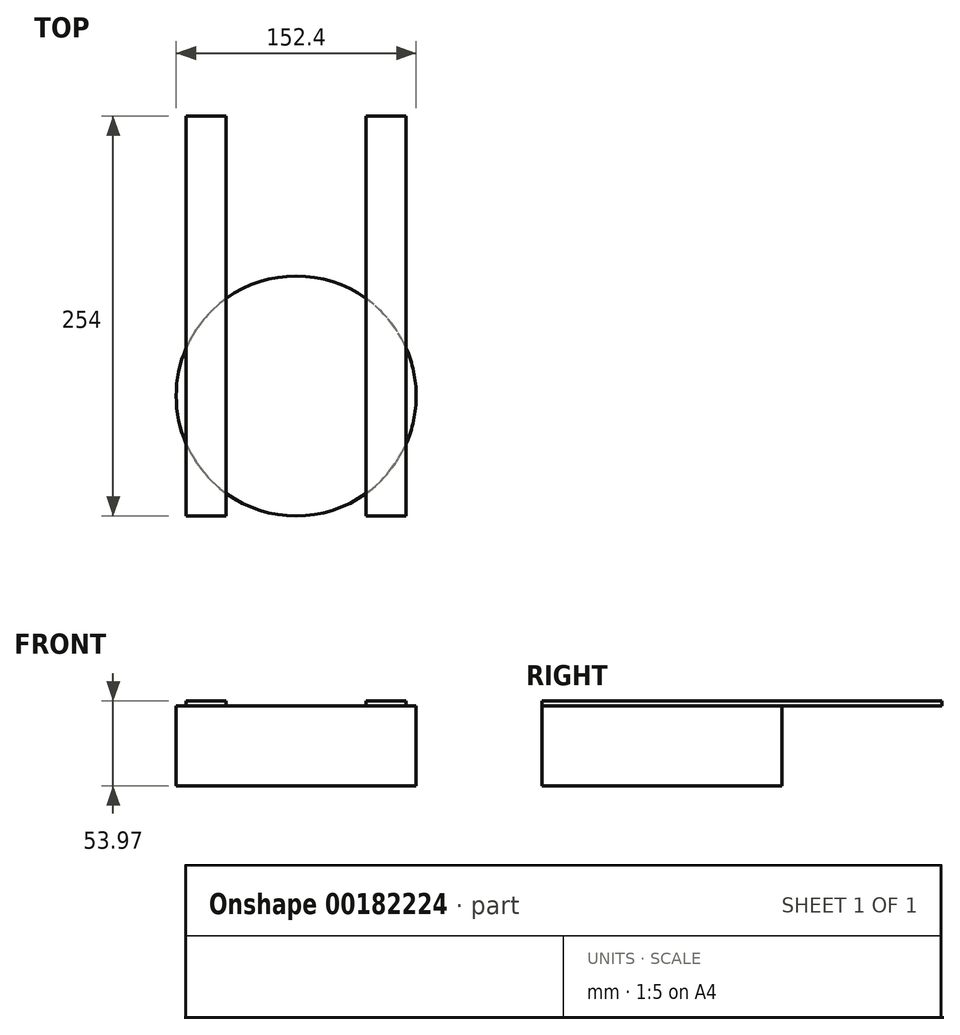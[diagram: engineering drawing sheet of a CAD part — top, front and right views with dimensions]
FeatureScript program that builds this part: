
annotation { "Feature Type Name" : "Feature", "Feature Type Description" : "" }
export const myFeature = defineFeature(function(context is Context, id is Id, definition is map)
    precondition{}
    {
        {
            var Q0;
            Q0=qCreatedBy(makeId("Top.planeOp"),FACE);
            var sketch = newSketch(context, id + "F0", { "sketchPlane" : qUnion([Q0])});
            skCircle(sketch, "E0", {"center": v(0, 0) * mm, "radius": 76.2 * mm});
            skSolve(sketch);
        }
        {
            var Q0;
            Q0=qSketchRegion(id+"F0",true);
            extrude(context, id + "F1", {"entities" : qUnion([Q0]), "oppositeDirection" : true, "depth" : 50.8 * mm});
        }
        {
            var Q0;
            Q0=qCreatedBy(makeId("Top.planeOp"),FACE);
            var sketch = newSketch(context, id + "F2", { "sketchPlane" : qUnion([Q0])});
            skLineSegment(sketch, "E1.bottom", {"start": v(-69.85, 177.8) * mm, "end": v(-44.45, 177.8) * mm});
            skLineSegment(sketch, "E1.top", {"start": v(-69.85, -76.2) * mm, "end": v(-44.45, -76.2) * mm});
            skLineSegment(sketch, "E1.left", {"start": v(-69.85, 177.8) * mm, "end": v(-69.85, -76.2) * mm});
            skLineSegment(sketch, "E1.right", {"start": v(-44.45, 177.8) * mm, "end": v(-44.45, -76.2) * mm});
            skLineSegment(sketch, "E2.bottom", {"start": v(44.45, -76.2) * mm, "end": v(69.85, -76.2) * mm});
            skLineSegment(sketch, "E2.top", {"start": v(44.45, 177.8) * mm, "end": v(69.85, 177.8) * mm});
            skLineSegment(sketch, "E2.left", {"start": v(44.45, -76.2) * mm, "end": v(44.45, 177.8) * mm});
            skLineSegment(sketch, "E2.right", {"start": v(69.85, -76.2) * mm, "end": v(69.85, 177.8) * mm});
            skSolve(sketch);
        }
        {
            var Q0;
            Q0=qSketchRegion(id+"F2",true);
            extrude(context, id + "F3", {"entities" : qUnion([Q0]), "operationType" : NewBodyOperationType.ADD, "depth" : 3.17 * mm});
        }
    });
